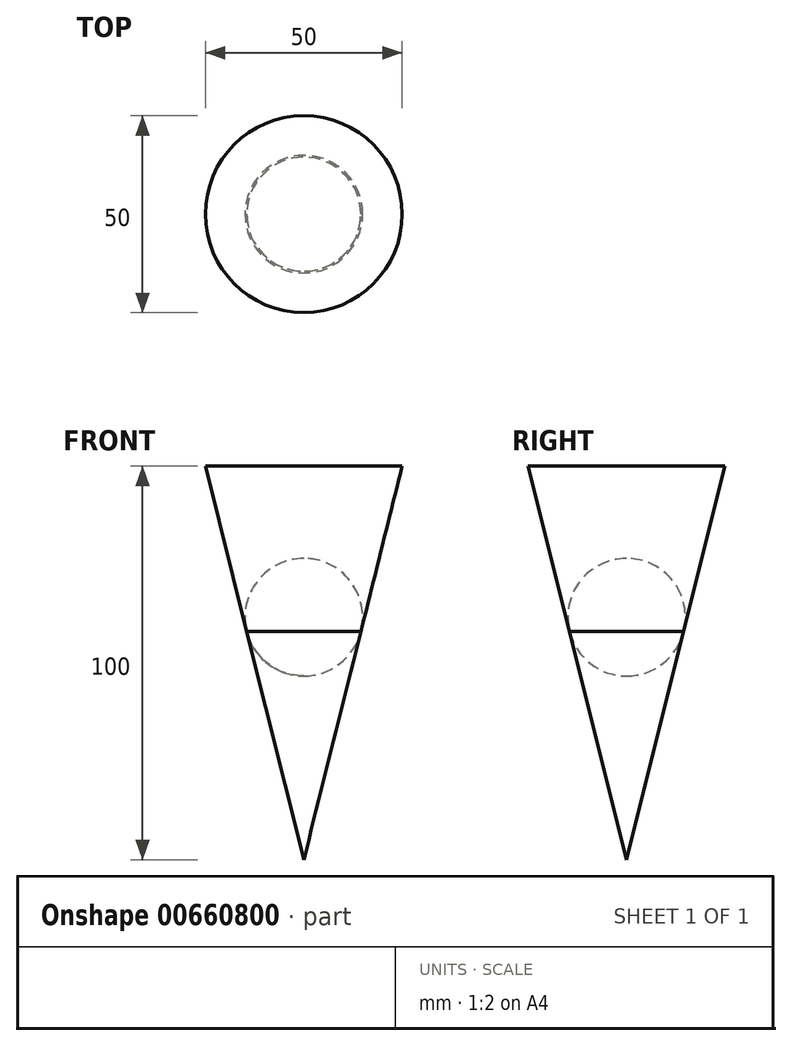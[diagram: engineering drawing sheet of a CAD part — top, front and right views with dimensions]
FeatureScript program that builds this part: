
annotation { "Feature Type Name" : "Feature", "Feature Type Description" : "" }
export const myFeature = defineFeature(function(context is Context, id is Id, definition is map)
    precondition{}
    {
        {
            var Q0;
            Q0=qCreatedBy(makeId("Front.planeOp"),FACE);
            var sketch = newSketch(context, id + "F0", { "sketchPlane" : qUnion([Q0])});
            skLineSegment(sketch, "E0", {"start": v(7.62, 40.18) * mm, "end": v(32.62, 40.18) * mm});
            skLineSegment(sketch, "E1", {"start": v(32.62, 40.18) * mm, "end": v(32.62, -59.82) * mm});
            skLineSegment(sketch, "E2", {"start": v(32.62, -59.82) * mm, "end": v(7.62, 40.18) * mm});
            skCircle(sketch, "E3", {"center": v(32.62, 1.8) * mm, "radius": 14.94 * mm});
            skSolve(sketch);
        }
        {
            var Q0;
            {var subQ0=sQuery(id+"F0.wireOp",EDGE,"E0");Q0=makeQuery(id+"F0.imprint","IMPRINT",FACE,{"disambiguationData":[TD([[makeQuery(id+"F0.imprint","IMPRINT",EDGE,{"derivedFrom":subQ0}),-1.0]])]});}
            var Q1;
            {var subQ0=sQuery(id+"F0.wireOp",EDGE,"E3");var subQ1=sQuery(id+"F0.wireOp",EDGE,"E1");var subQ2=makeQuery(id+"F0.imprint","INTERSECT",VERTEX,{"disambiguationData":[OD(0.0)],"derivedFrom":[subQ1,subQ0]});Q1=makeQuery(id+"F0.imprint","IMPRINT",FACE,{"disambiguationData":[TD([[makeQuery(id+"F0.imprint","IMPRINT",EDGE,{"disambiguationData":[TD([[subQ2,-1.0]])],"derivedFrom":subQ1}),-1.0]])]});}
            var Q2;
            Q2=sQuery(id+"F0.wireOp",EDGE,"E1");
            revolve(context, id + "F1", {"entities" : qUnion([Q0, Q1]), "axis" : qUnion([Q2]), "revolveType" : RevolveType.FULL});
        }
    });
